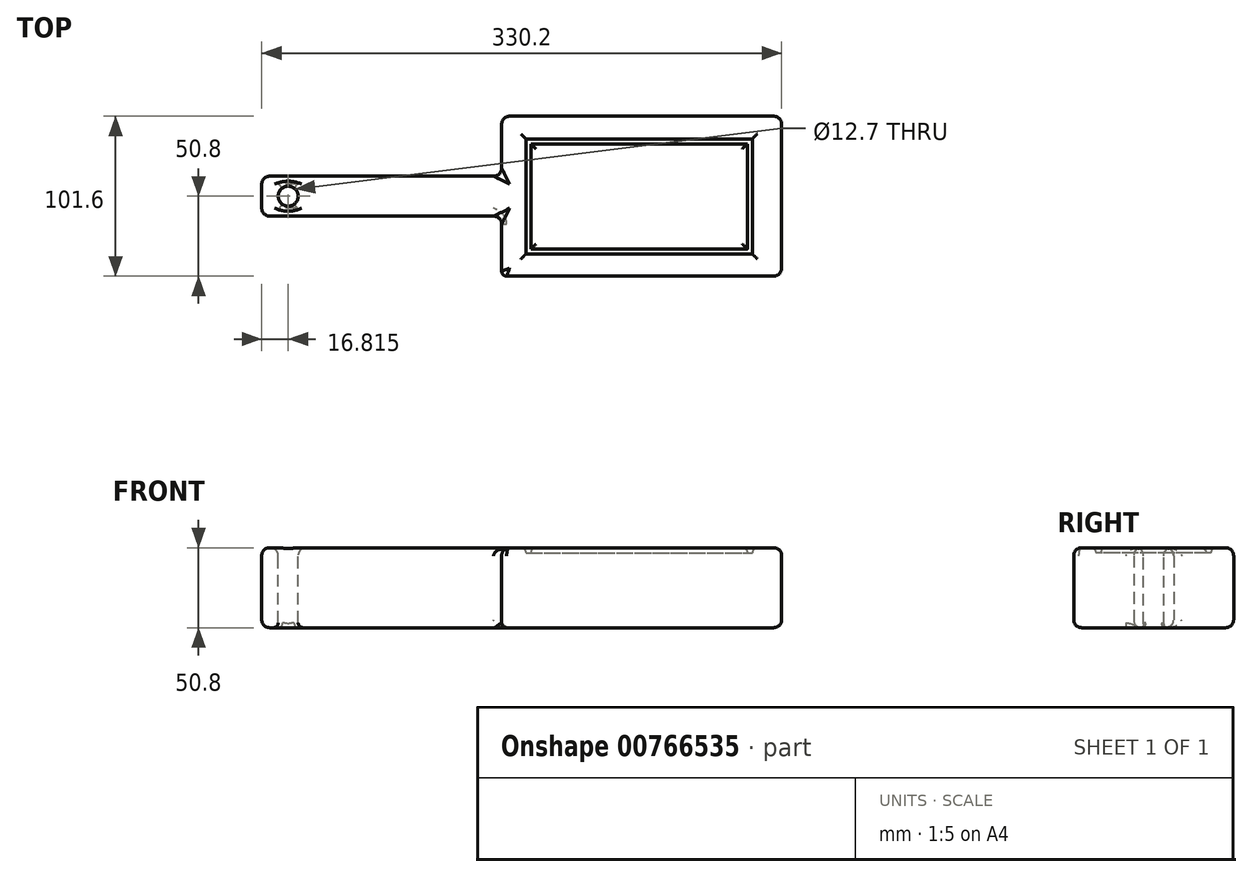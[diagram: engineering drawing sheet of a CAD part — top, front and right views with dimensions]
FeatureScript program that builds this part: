
annotation { "Feature Type Name" : "Feature", "Feature Type Description" : "" }
export const myFeature = defineFeature(function(context is Context, id is Id, definition is map)
    precondition{}
    {
        {
            var Q0;
            Q0=qCreatedBy(makeId("Top.planeOp"),FACE);
            var sketch = newSketch(context, id + "F0", { "sketchPlane" : qUnion([Q0])});
            skLineSegment(sketch, "E0.bottom", {"start": v(0, 0) * mm, "end": v(177.8, 0) * mm});
            skLineSegment(sketch, "E0.top", {"start": v(0, 101.6) * mm, "end": v(177.8, 101.6) * mm});
            skLineSegment(sketch, "E0.left", {"start": v(0, 0) * mm, "end": v(0, 101.6) * mm});
            skLineSegment(sketch, "E0.right", {"start": v(177.8, 0) * mm, "end": v(177.8, 101.6) * mm});
            skLineSegment(sketch, "E1.bottom", {"start": v(0, 63.5) * mm, "end": v(-152.4, 63.5) * mm});
            skLineSegment(sketch, "E1.top", {"start": v(0, 38.1) * mm, "end": v(-152.4, 38.1) * mm});
            skLineSegment(sketch, "E1.left", {"start": v(0, 63.5) * mm, "end": v(0, 38.1) * mm});
            skLineSegment(sketch, "E1.right", {"start": v(-152.4, 63.5) * mm, "end": v(-152.4, 38.1) * mm});
            skSolve(sketch);
        }
        {
            var Q0;
            Q0 = qSketchRegion(id + "F0", true);
            extrude(context, id + "F1", {"entities" : qUnion([Q0]), "depth" : 25.4 * mm, "offsetDistance" : 25.4 * mm});
        }
        {
            var Q0;
            Q0=makeQuery(id+"F1.opExtrude","CAP_FACE",FACE,{"disambiguationData":[OSD([sQuery(id+"F0.wireOp",EDGE,"E0.bottom"),sQuery(id+"F0.wireOp",EDGE,"E0.top"),sQuery(id+"F0.wireOp",EDGE,"E0.left"),sQuery(id+"F0.wireOp",EDGE,"E0.right"),sQuery(id+"F0.wireOp",EDGE,"E1.bottom"),sQuery(id+"F0.wireOp",EDGE,"E1.top"),sQuery(id+"F0.wireOp",EDGE,"E1.right")])],"isStart":false});
            extrude(context, id + "F2", {"entities" : qUnion([Q0]), "operationType" : NewBodyOperationType.ADD, "depth" : 25.4 * mm, "offsetDistance" : 25.4 * mm});
        }
        {
            var Q0;
            Q0=makeQuery(id+"F2.opExtrude","CAP_FACE",FACE,{"disambiguationData":[OSD([sQuery(id+"F0.wireOp",EDGE,"E0.bottom"),sQuery(id+"F0.wireOp",EDGE,"E0.top"),sQuery(id+"F0.wireOp",EDGE,"E0.left"),sQuery(id+"F0.wireOp",EDGE,"E0.right"),sQuery(id+"F0.wireOp",EDGE,"E1.bottom"),sQuery(id+"F0.wireOp",EDGE,"E1.top"),sQuery(id+"F0.wireOp",EDGE,"E1.right")])],"isStart":false});
            var sketch = newSketch(context, id + "F3", { "sketchPlane" : qUnion([Q0])});
            skCircle(sketch, "E2", {"center": v(-135.58, 50.8) * mm, "radius": 6.35 * mm});
            skSolve(sketch);
        }
        {
            var Q0;
            Q0 = qSketchRegion(id + "F3", true);
            extrude(context, id + "F4", {"entities" : qUnion([Q0]), "operationType" : NewBodyOperationType.REMOVE, "endBound" : BoundingType.THROUGH_ALL, "oppositeDirection" : true, "depth" : 25.4 * mm, "offsetDistance" : 25.4 * mm});
        }
        {
            var Q0;
            Q0=makeQuery(id+"F2.opExtrude","CAP_EDGE",EDGE,{"disambiguationData":[OSD([sQuery(id+"F0.wireOp",EDGE,"E0.top")])],"isStart":false});
            fillet(context, id + "F5", {"entities" : qUnion([Q0]), "radius" : 5.08 * mm, "tangentPropagation" : true, "allowEdgeOverflow" : false});
        }
        {
            var Q0;
            Q0=makeQuery(id+"F1.opExtrude","CAP_EDGE",EDGE,{"disambiguationData":[OSD([sQuery(id+"F0.wireOp",EDGE,"E1.bottom")])],"isStart":true});
            var Q1;
            Q1=makeQuery(id+"F2.opExtrude","CAP_FACE",FACE,{"disambiguationData":[OSD([sQuery(id+"F0.wireOp",EDGE,"E0.bottom"),sQuery(id+"F0.wireOp",EDGE,"E0.top"),sQuery(id+"F0.wireOp",EDGE,"E0.left"),sQuery(id+"F0.wireOp",EDGE,"E0.right"),sQuery(id+"F0.wireOp",EDGE,"E1.bottom"),sQuery(id+"F0.wireOp",EDGE,"E1.top"),sQuery(id+"F0.wireOp",EDGE,"E1.right")])],"isStart":false});
            var Q2;
            {var subQ0=sQuery(id+"F0.wireOp",EDGE,"E1.right");var subQ1=sQuery(id+"F0.wireOp",EDGE,"E1.bottom");Q2=makeQuery(id+"F2.boolean.opBoolean","MERGE",EDGE,{"derivedFrom":[makeQuery(id+"F1.opExtrude","SWEPT_EDGE",EDGE,{"disambiguationData":[OSD([subQ1,subQ0])]}),makeQuery(id+"F2.opExtrude","SWEPT_EDGE",EDGE,{"disambiguationData":[OSD([subQ1,subQ0])]})]});}
            var Q3;
            Q3=makeQuery(id+"F2.opExtrude","CAP_EDGE",EDGE,{"disambiguationData":[OSD([sQuery(id+"F0.wireOp",EDGE,"E0.bottom")])],"isStart":false});
            var Q4;
            Q4=makeQuery(id+"F1.opExtrude","CAP_EDGE",EDGE,{"disambiguationData":[OSD([sQuery(id+"F0.wireOp",EDGE,"E0.bottom")])],"isStart":true});
            var Q5;
            Q5=makeQuery(id+"F1.opExtrude","CAP_EDGE",EDGE,{"disambiguationData":[OSD([sQuery(id+"F0.wireOp",EDGE,"E1.top")])],"isStart":true});
            fillet(context, id + "F6", {"entities" : qUnion([Q0, Q1, Q2, Q3, Q4, Q5]), "radius" : 5.08 * mm, "tangentPropagation" : true, "allowEdgeOverflow" : false});
        }
        {
            var Q0;
            Q0=makeQuery(id+"F1.opExtrude","CAP_EDGE",EDGE,{"disambiguationData":[OSD([sQuery(id+"F0.wireOp",EDGE,"E1.right")])],"isStart":true});
            var Q1;
            Q1=makeQuery(id+"F1.opExtrude","CAP_EDGE",EDGE,{"disambiguationData":[OSD([sQuery(id+"F0.wireOp",EDGE,"E0.right")])],"isStart":true});
            var Q2;
            Q2=makeQuery(id+"F1.opExtrude","CAP_EDGE",EDGE,{"disambiguationData":[OSD([sQuery(id+"F0.wireOp",EDGE,"E0.top")])],"isStart":true});
            var Q3;
            {var subQ0=sQuery(id+"F0.wireOp",EDGE,"E0.right");var subQ1=sQuery(id+"F0.wireOp",EDGE,"E0.top");Q3=makeQuery(id+"F6.opFillet","BLEND_EDGE",EDGE,{"blendedFrom":[makeQuery(id+"F2.boolean.opBoolean","MERGE",EDGE,{"derivedFrom":[makeQuery(id+"F1.opExtrude","SWEPT_EDGE",EDGE,{"disambiguationData":[OSD([subQ1,subQ0])]}),makeQuery(id+"F2.opExtrude","SWEPT_EDGE",EDGE,{"disambiguationData":[OSD([subQ1,subQ0])]})]}),makeQuery(id+"F1.opExtrude","CAP_FACE",FACE,{"disambiguationData":[OSD([sQuery(id+"F0.wireOp",EDGE,"E0.bottom"),subQ1,sQuery(id+"F0.wireOp",EDGE,"E0.left"),subQ0,sQuery(id+"F0.wireOp",EDGE,"E1.bottom"),sQuery(id+"F0.wireOp",EDGE,"E1.top"),sQuery(id+"F0.wireOp",EDGE,"E1.right")])],"isStart":true})],"blendedInto":[makeQuery(id+"F1.opExtrude","CAP_FACE",FACE,{"disambiguationData":[OSD([sQuery(id+"F0.wireOp",EDGE,"E0.bottom"),subQ1,sQuery(id+"F0.wireOp",EDGE,"E0.left"),subQ0,sQuery(id+"F0.wireOp",EDGE,"E1.bottom"),sQuery(id+"F0.wireOp",EDGE,"E1.top"),sQuery(id+"F0.wireOp",EDGE,"E1.right")])],"isStart":true})]});}
            fillet(context, id + "F7", {"entities" : qUnion([Q0, Q1, Q2, Q3]), "radius" : 5.08 * mm, "tangentPropagation" : true, "allowEdgeOverflow" : false});
        }
        {
            var Q0;
            Q0=makeQuery(id+"F6.opFillet","SPLIT",FACE,{"disambiguationData":[OD(0.0)],"derivedFrom":makeQuery(id+"F2.opExtrude","CAP_FACE",FACE,{"disambiguationData":[OSD([sQuery(id+"F0.wireOp",EDGE,"E0.bottom"),sQuery(id+"F0.wireOp",EDGE,"E0.top"),sQuery(id+"F0.wireOp",EDGE,"E0.left"),sQuery(id+"F0.wireOp",EDGE,"E0.right"),sQuery(id+"F0.wireOp",EDGE,"E1.bottom"),sQuery(id+"F0.wireOp",EDGE,"E1.top"),sQuery(id+"F0.wireOp",EDGE,"E1.right")])],"isStart":false})});
            var sketch = newSketch(context, id + "F8", { "sketchPlane" : qUnion([Q0])});
            skLineSegment(sketch, "E3.bottom", {"start": v(15.34, 87.2) * mm, "end": v(159.2, 87.2) * mm});
            skLineSegment(sketch, "E3.top", {"start": v(15.34, 14.02) * mm, "end": v(159.2, 14.02) * mm});
            skLineSegment(sketch, "E3.left", {"start": v(15.34, 87.2) * mm, "end": v(15.34, 14.02) * mm});
            skLineSegment(sketch, "E3.right", {"start": v(159.2, 87.2) * mm, "end": v(159.2, 14.02) * mm});
            skLineSegment(sketch, "E4.0", {"start": v(18.52, 84.02) * mm, "end": v(156.03, 84.02) * mm});
            skLineSegment(sketch, "E4.1", {"start": v(18.52, 84.02) * mm, "end": v(18.52, 17.2) * mm});
            skLineSegment(sketch, "E4.2", {"start": v(18.52, 17.2) * mm, "end": v(156.03, 17.2) * mm});
            skLineSegment(sketch, "E4.3", {"start": v(156.03, 84.02) * mm, "end": v(156.03, 17.2) * mm});
            skSolve(sketch);
        }
        {
            var Q0;
            Q0 = qSketchRegion(id + "F8", true);
            extrude(context, id + "F9", {"entities" : qUnion([Q0]), "operationType" : NewBodyOperationType.REMOVE, "oppositeDirection" : true, "depth" : 3.17 * mm, "offsetDistance" : 25.4 * mm});
        }
        {
            var Q0;
            {var subQ0=sQuery(id+"F0.wireOp",EDGE,"E1.left");var subQ1=sQuery(id+"F0.wireOp",EDGE,"E1.top");var subQ2=sQuery(id+"F0.wireOp",EDGE,"E0.left");Q0=makeQuery(id+"F2.boolean.opBoolean","MERGE",EDGE,{"derivedFrom":[makeQuery(id+"F1.opExtrude","SWEPT_EDGE",EDGE,{"disambiguationData":[OSD([subQ2,subQ1,subQ0])]}),makeQuery(id+"F2.opExtrude","SWEPT_EDGE",EDGE,{"disambiguationData":[OSD([subQ2,subQ1,subQ0])]})]});}
            fillet(context, id + "F10", {"entities" : qUnion([Q0]), "radius" : 5.08 * mm, "tangentPropagation" : true, "allowEdgeOverflow" : false});
        }
        {
            var Q0;
            {var subQ0=sQuery(id+"F0.wireOp",EDGE,"E1.left");var subQ1=sQuery(id+"F0.wireOp",EDGE,"E1.bottom");var subQ2=sQuery(id+"F0.wireOp",EDGE,"E0.left");Q0=makeQuery(id+"F2.boolean.opBoolean","MERGE",EDGE,{"derivedFrom":[makeQuery(id+"F1.opExtrude","SWEPT_EDGE",EDGE,{"disambiguationData":[OSD([subQ2,subQ1,subQ0])]}),makeQuery(id+"F2.opExtrude","SWEPT_EDGE",EDGE,{"disambiguationData":[OSD([subQ2,subQ1,subQ0])]})]});}
            fillet(context, id + "F11", {"entities" : qUnion([Q0]), "radius" : 5.08 * mm, "tangentPropagation" : true, "allowEdgeOverflow" : false});
        }
        {
            var Q0;
            Q0=makeQuery(id+"F9.boolean.opBoolean","SPLIT",FACE,{"disambiguationData":[TD([makeQuery(id+"F9.opExtrude","SWEPT_FACE",FACE,{"disambiguationData":[OSD([sQuery(id+"F8.wireOp",EDGE,"E4.0")])]})])],"derivedFrom":makeQuery(id+"F6.opFillet","SPLIT",FACE,{"disambiguationData":[OD(0.0)],"derivedFrom":makeQuery(id+"F2.opExtrude","CAP_FACE",FACE,{"disambiguationData":[OSD([sQuery(id+"F0.wireOp",EDGE,"E0.bottom"),sQuery(id+"F0.wireOp",EDGE,"E0.top"),sQuery(id+"F0.wireOp",EDGE,"E0.left"),sQuery(id+"F0.wireOp",EDGE,"E0.right"),sQuery(id+"F0.wireOp",EDGE,"E1.bottom"),sQuery(id+"F0.wireOp",EDGE,"E1.top"),sQuery(id+"F0.wireOp",EDGE,"E1.right")])],"isStart":false})})});
            var Q1;
            {var subQ0=sQuery(id+"F0.wireOp",EDGE,"E0.right");var subQ1=sQuery(id+"F0.wireOp",EDGE,"E0.top");var subQ3=sQuery(id+"F0.wireOp",EDGE,"E0.left");var subQ5=sQuery(id+"F0.wireOp",EDGE,"E1.bottom");var subQ8=sQuery(id+"F0.wireOp",EDGE,"E1.top");var subQ9=sQuery(id+"F0.wireOp",EDGE,"E0.bottom");Q1=makeQuery(id+"F9.boolean.opBoolean","SPLIT",FACE,{"disambiguationData":[TD([makeQuery(id+"F5.opFillet","BLEND_FACE",FACE,{"disambiguationData":[OSD([subQ1])]})])],"derivedFrom":makeQuery(id+"F6.opFillet","SPLIT",FACE,{"disambiguationData":[OD(0.0)],"derivedFrom":makeQuery(id+"F2.opExtrude","CAP_FACE",FACE,{"disambiguationData":[OSD([subQ9,subQ1,subQ3,subQ0,subQ5,subQ8,sQuery(id+"F0.wireOp",EDGE,"E1.right")])],"isStart":false})})});}
            var Q2;
            Q2=makeQuery(id+"F1.opExtrude","CAP_FACE",FACE,{"disambiguationData":[OSD([sQuery(id+"F0.wireOp",EDGE,"E0.bottom"),sQuery(id+"F0.wireOp",EDGE,"E0.top"),sQuery(id+"F0.wireOp",EDGE,"E0.left"),sQuery(id+"F0.wireOp",EDGE,"E0.right"),sQuery(id+"F0.wireOp",EDGE,"E1.bottom"),sQuery(id+"F0.wireOp",EDGE,"E1.top"),sQuery(id+"F0.wireOp",EDGE,"E1.right")])],"isStart":true});
            fillet(context, id + "F12", {"entities" : qUnion([Q0, Q1, Q2]), "radius" : 3.17 * mm, "tangentPropagation" : true, "allowEdgeOverflow" : false});
        }
    });
